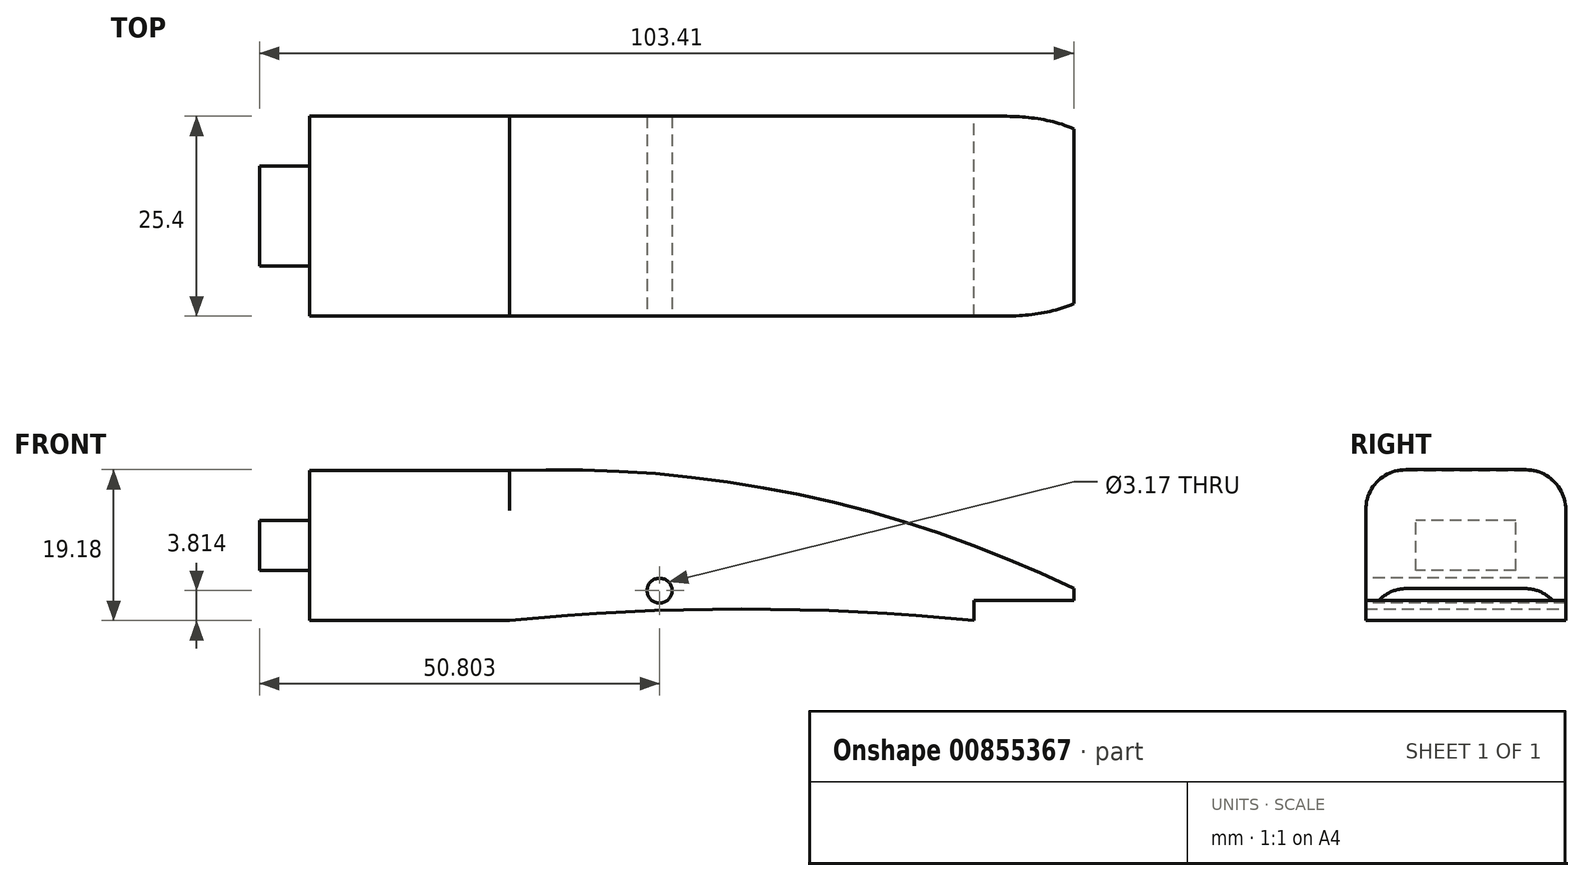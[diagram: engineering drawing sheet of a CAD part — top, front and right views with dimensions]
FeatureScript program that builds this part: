
annotation { "Feature Type Name" : "Feature", "Feature Type Description" : "" }
export const myFeature = defineFeature(function(context is Context, id is Id, definition is map)
    precondition{}
    {
        {
            var Q0;
            Q0=qCreatedBy(makeId("Front.planeOp"),FACE);
            var sketch = newSketch(context, id + "F0", { "sketchPlane" : qUnion([Q0])});
            skLineSegment(sketch, "E0", {"start": v(61.51, 7.85) * mm, "end": v(61.51, 7.09) * mm});
            skLineSegment(sketch, "E1", {"start": v(25.68, 5.82) * mm, "end": v(25.68, 15.34) * mm});
            skArc(sketch, "E2", {"start": v(61.51, 7.85) * mm, "mid": v(44.06, 13.82) * mm, "end": v(25.68, 15.34) * mm});
            skArc(sketch, "E3", {"start": v(55.16, 5.82) * mm, "mid": v(40.42, 6.55) * mm, "end": v(25.68, 5.82) * mm});
            skLineSegment(sketch, "E4", {"start": v(55.16, 5.82) * mm, "end": v(55.16, 7.09) * mm});
            skLineSegment(sketch, "E5", {"start": v(55.16, 7.09) * mm, "end": v(61.51, 7.09) * mm});
            skSolve(sketch);
        }
        {
            var Q0;
            Q0=makeQuery(id+"F0.imprint","IMPRINT",FACE,{"disambiguationData":[TD([[makeQuery(id+"F0.imprint","IMPRINT",EDGE,{"derivedFrom":sQuery(id+"F0.wireOp",EDGE,"E0")}),-1.0]])]});
            extrude(context, id + "F1", {"entities" : qUnion([Q0]), "depth" : 12.7 * mm, "offsetDistance" : 25.4 * mm});
        }
        {
            var Q0;
            Q0=makeQuery(id+"F1.opExtrude","CAP_EDGE",EDGE,{"disambiguationData":[OSD([sQuery(id+"F0.wireOp",EDGE,"E2")])],"isStart":false});
            var Q1;
            Q1=makeQuery(id+"F1.opExtrude","CAP_EDGE",EDGE,{"disambiguationData":[OSD([sQuery(id+"F0.wireOp",EDGE,"E2")])],"isStart":true});
            fillet(context, id + "F2", {"entities" : qUnion([Q0, Q1]), "radius" : 2.54 * mm, "tangentPropagation" : true, "allowEdgeOverflow" : false});
        }
        {
            var Q0;
            Q0=makeQuery(id+"F1.opExtrude","SWEPT_FACE",FACE,{"disambiguationData":[OSD([sQuery(id+"F0.wireOp",EDGE,"E1")])]});
            extrude(context, id + "F3", {"entities" : qUnion([Q0]), "operationType" : NewBodyOperationType.ADD, "depth" : 12.7 * mm, "offsetDistance" : 25.4 * mm});
        }
        {
            var Q0;
            Q0=makeQuery(id+"F1.opExtrude","SWEPT_BODY",BODY,{"disambiguationData":[OSD([sQuery(id+"F0.wireOp",EDGE,"E0"),sQuery(id+"F0.wireOp",EDGE,"E1"),sQuery(id+"F0.wireOp",EDGE,"E2"),sQuery(id+"F0.wireOp",EDGE,"E3"),sQuery(id+"F0.wireOp",EDGE,"E4"),sQuery(id+"F0.wireOp",EDGE,"E5")])]});
            var Q1;
            Q1=qCreatedBy(makeId("Origin.pointOp"),VERTEX);
            transform(context, id + "F4", {"entities" : qUnion([Q0]), "transformType" : TransformType.SCALE_UNIFORMLY, "scale" : 2, "scalePoint" : qUnion([Q1]), "makeCopy" : false});
        }
        {
            var Q0;
            Q0=makeQuery(id+"F3.opExtrude","CAP_FACE",FACE,{"disambiguationData":[OSD([sQuery(id+"F0.wireOp",EDGE,"E1")])],"isStart":false});
            var sketch = newSketch(context, id + "F5", { "sketchPlane" : qUnion([Q0])});
            skLineSegment(sketch, "E6.bottom", {"start": v(6.35, 17.98) * mm, "end": v(19.05, 17.98) * mm});
            skLineSegment(sketch, "E6.top", {"start": v(6.35, 24.33) * mm, "end": v(19.05, 24.33) * mm});
            skLineSegment(sketch, "E6.left", {"start": v(6.35, 17.98) * mm, "end": v(6.35, 24.33) * mm});
            skLineSegment(sketch, "E6.right", {"start": v(19.05, 17.98) * mm, "end": v(19.05, 24.33) * mm});
            skSolve(sketch);
        }
        {
            var Q0;
            Q0=makeQuery(id+"F5.imprint","IMPRINT",FACE,{"disambiguationData":[TD([[makeQuery(id+"F5.imprint","IMPRINT",EDGE,{"derivedFrom":sQuery(id+"F5.wireOp",EDGE,"E6.bottom")}),1.0]])]});
            extrude(context, id + "F6", {"entities" : qUnion([Q0]), "operationType" : NewBodyOperationType.ADD, "depth" : 6.35 * mm, "offsetDistance" : 25.4 * mm});
        }
        {
            var Q0;
            {var subQ0=sQuery(id+"F0.wireOp",EDGE,"E1");Q0=makeQuery(id+"F3.boolean.opBoolean","MERGE",FACE,{"derivedFrom":[makeQuery(id+"F1.opExtrude","CAP_FACE",FACE,{"disambiguationData":[OSD([sQuery(id+"F0.wireOp",EDGE,"E0"),subQ0,sQuery(id+"F0.wireOp",EDGE,"E2"),sQuery(id+"F0.wireOp",EDGE,"E3"),sQuery(id+"F0.wireOp",EDGE,"E4"),sQuery(id+"F0.wireOp",EDGE,"E5")])],"isStart":false}),makeQuery(id+"F3.opExtrude","SWEPT_FACE",FACE,{"disambiguationData":[OSD([subQ0]),TDD([makeQuery(id+"F1.opExtrude","CAP_EDGE",EDGE,{"disambiguationData":[OSD([subQ0])],"isStart":false})])]})]});}
            var sketch = newSketch(context, id + "F7", { "sketchPlane" : qUnion([Q0])});
            skCircle(sketch, "E7", {"center": v(70.41, 15.44) * mm, "radius": 1.59 * mm});
            skSolve(sketch);
        }
        {
            var Q0;
            Q0=makeQuery(id+"F7.imprint","IMPRINT",FACE,{"disambiguationData":[TD([[makeQuery(id+"F7.imprint","IMPRINT",EDGE,{"derivedFrom":sQuery(id+"F7.wireOp",EDGE,"E7")}),1.0]])]});
            extrude(context, id + "F8", {"entities" : qUnion([Q0]), "operationType" : NewBodyOperationType.REMOVE, "oppositeDirection" : true, "depth" : 25.4 * mm, "offsetDistance" : 25.4 * mm});
        }
    });
